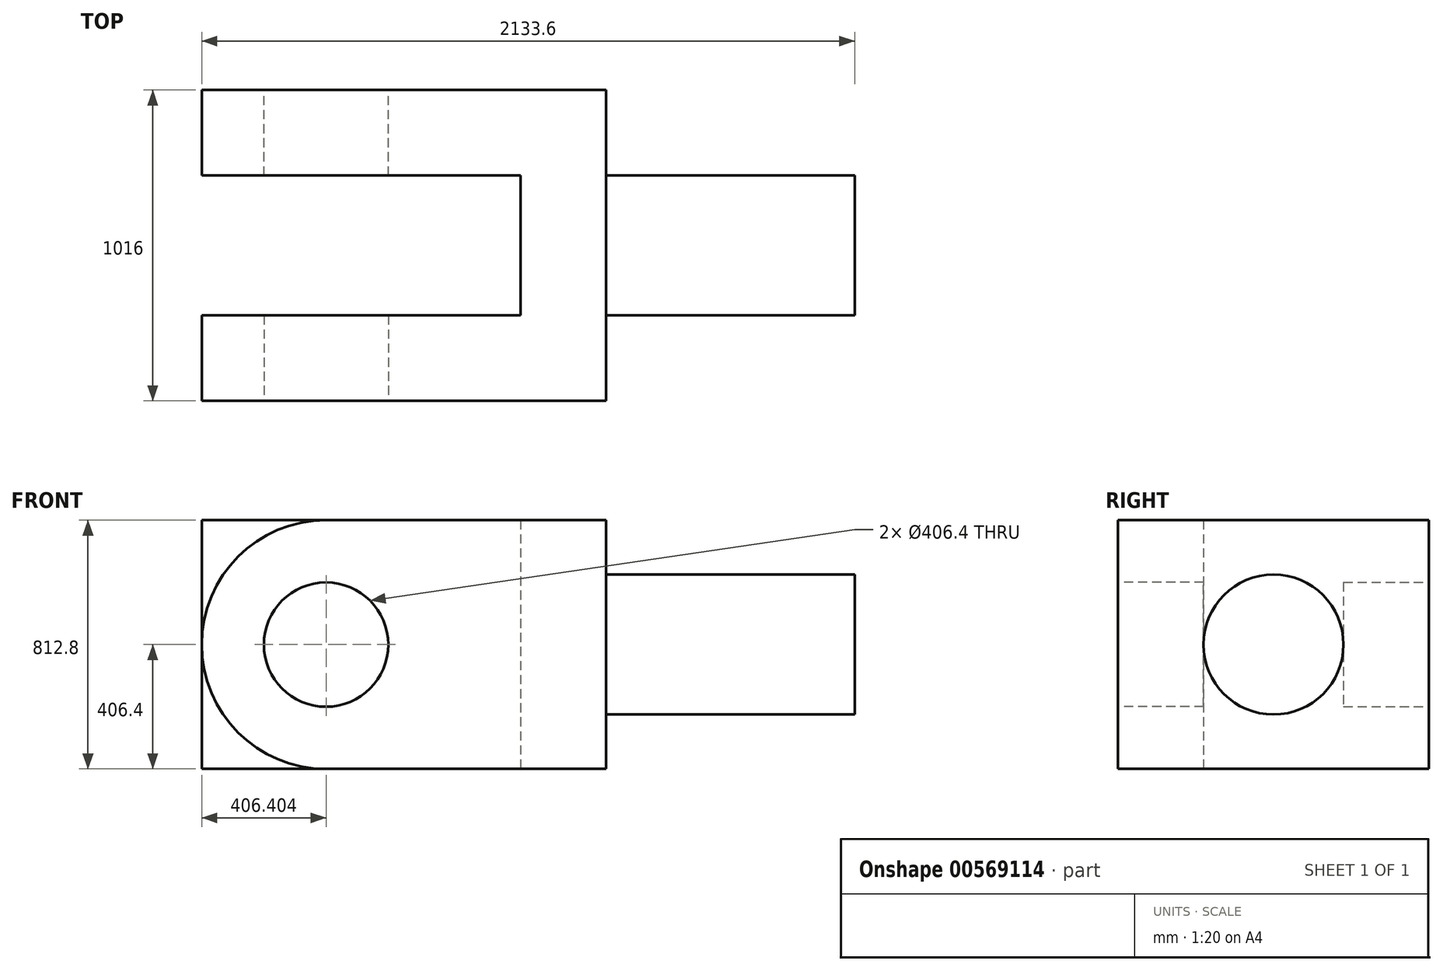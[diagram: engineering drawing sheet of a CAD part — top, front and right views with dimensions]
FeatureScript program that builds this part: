
annotation { "Feature Type Name" : "Feature", "Feature Type Description" : "" }
export const myFeature = defineFeature(function(context is Context, id is Id, definition is map)
    precondition{}
    {
        {
            var Q0;
            Q0=qCreatedBy(makeId("Top.planeOp"),FACE);
            var sketch = newSketch(context, id + "F0", { "sketchPlane" : qUnion([Q0])});
            skLineSegment(sketch, "E0", {"start": v(-654.94, 435.58) * mm, "end": v(-654.94, 156.18) * mm});
            skLineSegment(sketch, "E1", {"start": v(-654.94, 156.18) * mm, "end": v(386.46, 156.18) * mm});
            skLineSegment(sketch, "E2", {"start": v(386.46, 156.18) * mm, "end": v(386.46, -301.02) * mm});
            skLineSegment(sketch, "E3", {"start": v(386.46, -301.02) * mm, "end": v(-654.94, -301.02) * mm});
            skLineSegment(sketch, "E4", {"start": v(-654.94, -301.02) * mm, "end": v(-654.94, -580.42) * mm});
            skLineSegment(sketch, "E5", {"start": v(-654.94, -580.42) * mm, "end": v(665.86, -580.42) * mm});
            skLineSegment(sketch, "E6", {"start": v(665.86, -580.42) * mm, "end": v(665.86, 435.58) * mm});
            skLineSegment(sketch, "E7", {"start": v(665.86, 435.58) * mm, "end": v(-654.94, 435.58) * mm});
            skLineSegment(sketch, "E8", {"start": v(665.86, 156.18) * mm, "end": v(1478.66, 156.18) * mm});
            skLineSegment(sketch, "E9", {"start": v(1478.66, 156.18) * mm, "end": v(1478.66, -301.02) * mm});
            skLineSegment(sketch, "E10", {"start": v(1478.66, -301.02) * mm, "end": v(665.86, -301.02) * mm});
            skSolve(sketch);
        }
        {
            var Q0;
            Q0=makeQuery(id+"F0.imprint","IMPRINT",FACE,{"disambiguationData":[TD([[makeQuery(id+"F0.imprint","IMPRINT",EDGE,{"derivedFrom":sQuery(id+"F0.wireOp",EDGE,"E0")}),1.0]])]});
            extrude(context, id + "F1", {"entities" : qUnion([Q0]), "depth" : 812.8 * mm, "offsetDistance" : 25.4 * mm});
        }
        {
            var Q0;
            Q0=makeQuery(id+"F1.opExtrude","SWEPT_FACE",FACE,{"disambiguationData":[OSD([sQuery(id+"F0.wireOp",EDGE,"E6")])]});
            var sketch = newSketch(context, id + "F2", { "sketchPlane" : qUnion([Q0])});
            skCircle(sketch, "E11", {"center": v(-72.42, 406.4) * mm, "radius": 228.6 * mm});
            skPoint(sketch, "E11.centerSnap0", {"position": v(-580.42, 406.4) * mm});
            skPoint(sketch, "E11.centerSnap1", {"position": v(-72.42, 812.8) * mm});
            skSolve(sketch);
        }
        {
            var Q0;
            Q0=makeQuery(id+"F2.imprint","IMPRINT",FACE,{"disambiguationData":[TD([[makeQuery(id+"F2.imprint","IMPRINT",EDGE,{"derivedFrom":sQuery(id+"F2.wireOp",EDGE,"E11")}),1.0]])]});
            extrude(context, id + "F3", {"entities" : qUnion([Q0]), "operationType" : NewBodyOperationType.ADD, "depth" : 812.8 * mm, "offsetDistance" : 25.4 * mm});
        }
        {
            var Q0;
            Q0=makeQuery(id+"F1.opExtrude","SWEPT_FACE",FACE,{"disambiguationData":[OSD([sQuery(id+"F0.wireOp",EDGE,"E5")])]});
            var sketch = newSketch(context, id + "F4", { "sketchPlane" : qUnion([Q0])});
            skCircle(sketch, "E12", {"center": v(-248.54, 406.4) * mm, "radius": 203.2 * mm});
            skArc(sketch, "E13", {"start": v(-248.54, 812.8) * mm, "mid": v(-654.94, 406.4) * mm, "end": v(-248.54, 0) * mm});
            skSolve(sketch);
        }
        {
            var Q0;
            {var subQ0=sQuery(id+"F4.wireOp",EDGE,"E13");var subQ1=sQuery(id+"F0.wireOp",EDGE,"E5");var subQ2=makeQuery(id+"F1.opExtrude","CAP_EDGE",EDGE,{"disambiguationData":[OSD([subQ1])],"isStart":false});var subQ3=makeQuery(id+"F4.imprint","INTERSECT",VERTEX,{"derivedFrom":[subQ2,subQ0]});Q0=makeQuery(id+"F4.imprint","IMPRINT",FACE,{"disambiguationData":[TD([[makeQuery(id+"F4.imprint","IMPRINT",EDGE,{"disambiguationData":[TD([[subQ3,-1.0]])],"derivedFrom":subQ0}),-1.0]])]});}
            var Q1;
            {var subQ0=sQuery(id+"F4.wireOp",EDGE,"E13");var subQ1=sQuery(id+"F0.wireOp",EDGE,"E5");var subQ2=makeQuery(id+"F1.opExtrude","CAP_EDGE",EDGE,{"disambiguationData":[OSD([subQ1])],"isStart":true});var subQ3=makeQuery(id+"F4.imprint","INTERSECT",VERTEX,{"derivedFrom":[subQ2,subQ0]});Q1=makeQuery(id+"F4.imprint","IMPRINT",FACE,{"disambiguationData":[TD([[makeQuery(id+"F4.imprint","IMPRINT",EDGE,{"disambiguationData":[TD([[subQ3,1.0]])],"derivedFrom":subQ0}),-1.0]])]});}
            var Q2;
            Q2=makeQuery(id+"F4.imprint","IMPRINT",FACE,{"disambiguationData":[TD([[makeQuery(id+"F4.imprint","IMPRINT",EDGE,{"derivedFrom":sQuery(id+"F4.wireOp",EDGE,"E12")}),1.0]])]});
            extrude(context, id + "F5", {"entities" : qUnion([Q0, Q1, Q2]), "operationType" : NewBodyOperationType.REMOVE, "oppositeDirection" : true, "depth" : 279.4 * mm, "offsetDistance" : 25.4 * mm});
        }
        {
            var Q0;
            Q0=makeQuery(id+"F1.opExtrude","SWEPT_FACE",FACE,{"disambiguationData":[OSD([sQuery(id+"F0.wireOp",EDGE,"E7")])]});
            var sketch = newSketch(context, id + "F6", { "sketchPlane" : qUnion([Q0])});
            skCircle(sketch, "E14", {"center": v(248.54, 406.4) * mm, "radius": 203.2 * mm});
            skArc(sketch, "E15", {"start": v(248.54, 812.8) * mm, "mid": v(654.94, 406.4) * mm, "end": v(248.54, 0) * mm});
            skSolve(sketch);
        }
        {
            var Q0;
            {var subQ0=sQuery(id+"F6.wireOp",EDGE,"E15");var subQ1=sQuery(id+"F0.wireOp",EDGE,"E7");var subQ2=makeQuery(id+"F1.opExtrude","CAP_EDGE",EDGE,{"disambiguationData":[OSD([subQ1])],"isStart":false});var subQ3=makeQuery(id+"F6.imprint","INTERSECT",VERTEX,{"derivedFrom":[subQ2,subQ0]});Q0=makeQuery(id+"F6.imprint","IMPRINT",FACE,{"disambiguationData":[TD([[makeQuery(id+"F6.imprint","IMPRINT",EDGE,{"disambiguationData":[TD([[subQ3,-1.0]])],"derivedFrom":subQ0}),1.0]])]});}
            var Q1;
            {var subQ0=sQuery(id+"F6.wireOp",EDGE,"E15");var subQ1=sQuery(id+"F0.wireOp",EDGE,"E7");var subQ2=makeQuery(id+"F1.opExtrude","CAP_EDGE",EDGE,{"disambiguationData":[OSD([subQ1])],"isStart":true});var subQ3=makeQuery(id+"F6.imprint","INTERSECT",VERTEX,{"derivedFrom":[subQ2,subQ0]});Q1=makeQuery(id+"F6.imprint","IMPRINT",FACE,{"disambiguationData":[TD([[makeQuery(id+"F6.imprint","IMPRINT",EDGE,{"disambiguationData":[TD([[subQ3,1.0]])],"derivedFrom":subQ0}),1.0]])]});}
            var Q2;
            Q2=makeQuery(id+"F6.imprint","IMPRINT",FACE,{"disambiguationData":[TD([[makeQuery(id+"F6.imprint","IMPRINT",EDGE,{"derivedFrom":sQuery(id+"F6.wireOp",EDGE,"E14")}),1.0]])]});
            extrude(context, id + "F7", {"entities" : qUnion([Q0, Q1, Q2]), "operationType" : NewBodyOperationType.REMOVE, "oppositeDirection" : true, "depth" : 279.4 * mm, "offsetDistance" : 25.4 * mm});
        }
    });
